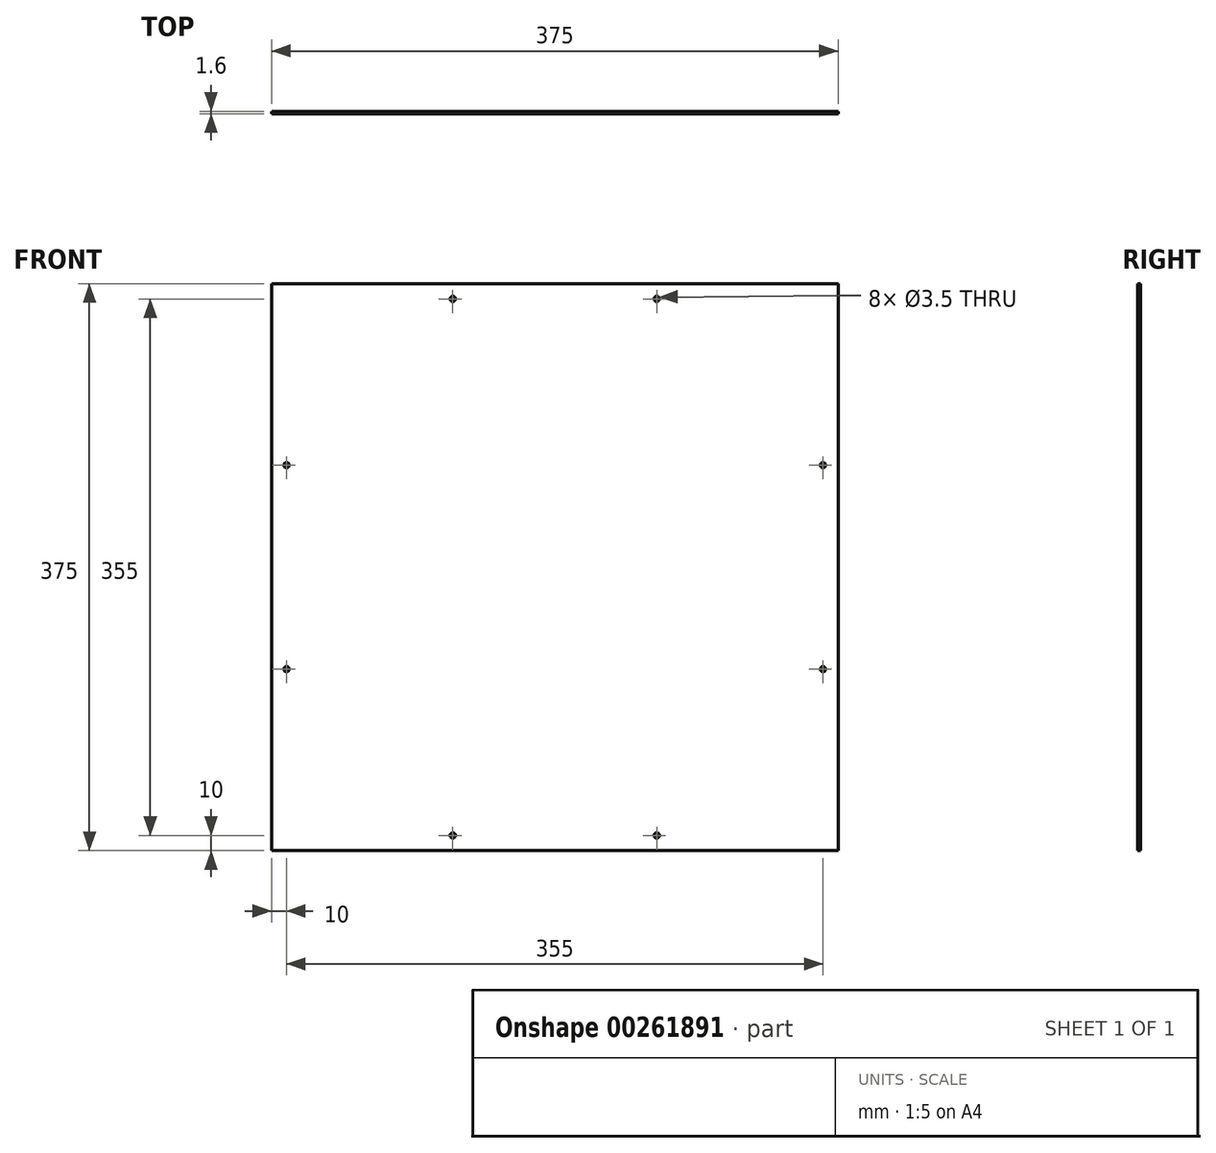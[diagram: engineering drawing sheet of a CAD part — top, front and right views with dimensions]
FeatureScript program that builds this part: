
annotation { "Feature Type Name" : "Feature", "Feature Type Description" : "" }
export const myFeature = defineFeature(function(context is Context, id is Id, definition is map)
    precondition{}
    {
        {
            var Q0;
            Q0=qCreatedBy(makeId("Front.planeOp"),FACE);
            var sketch = newSketch(context, id + "F0", { "sketchPlane" : qUnion([Q0])});
            skLineSegment(sketch, "E0.bottom", {"start": v(0, 0) * mm, "end": v(-375, 0) * mm});
            skLineSegment(sketch, "E0.top", {"start": v(0, 375) * mm, "end": v(-375, 375) * mm});
            skLineSegment(sketch, "E0.left", {"start": v(0, 0) * mm, "end": v(0, 375) * mm});
            skLineSegment(sketch, "E0.right", {"start": v(-375, 0) * mm, "end": v(-375, 375) * mm});
            skSolve(sketch);
        }
        {
            var Q0;
            Q0=makeQuery(id+"F0.imprint","IMPRINT",FACE,{"disambiguationData":[TD([[makeQuery(id+"F0.imprint","IMPRINT",EDGE,{"derivedFrom":sQuery(id+"F0.wireOp",EDGE,"E0.bottom")}),-1.0]])]});
            extrude(context, id + "F1", {"entities" : qUnion([Q0]), "depth" : 1.6 * mm});
        }
        {
            var Q0;
            Q0=makeQuery(id+"F1.opExtrude","CAP_FACE",FACE,{"disambiguationData":[OSD([sQuery(id+"F0.wireOp",EDGE,"E0.bottom"),sQuery(id+"F0.wireOp",EDGE,"E0.top"),sQuery(id+"F0.wireOp",EDGE,"E0.left"),sQuery(id+"F0.wireOp",EDGE,"E0.right")])],"isStart":false});
            var sketch = newSketch(context, id + "F2", { "sketchPlane" : qUnion([Q0])});
            skLineSegment(sketch, "E1.0.0", {"start": v(0, 0) * mm, "end": v(0, 375) * mm});
            skLineSegment(sketch, "E1.0.1", {"start": v(0, 375) * mm, "end": v(-375, 375) * mm});
            skLineSegment(sketch, "E1.0.2", {"start": v(-375, 375) * mm, "end": v(-375, 0) * mm});
            skLineSegment(sketch, "E1.0.3", {"start": v(-375, 0) * mm, "end": v(0, 0) * mm});
            skCircle(sketch, "E2", {"center": v(-10, 120) * mm, "radius": 1.75 * mm});
            skCircle(sketch, "E3", {"center": v(-10, 255) * mm, "radius": 1.75 * mm});
            skCircle(sketch, "E4", {"center": v(-120, 365) * mm, "radius": 1.75 * mm});
            skCircle(sketch, "E5", {"center": v(-255, 365) * mm, "radius": 1.75 * mm});
            skCircle(sketch, "E6", {"center": v(-365, 255) * mm, "radius": 1.75 * mm});
            skCircle(sketch, "E7", {"center": v(-365, 120) * mm, "radius": 1.75 * mm});
            skCircle(sketch, "E8", {"center": v(-255, 10) * mm, "radius": 1.75 * mm});
            skCircle(sketch, "E9", {"center": v(-120, 10) * mm, "radius": 1.75 * mm});
            skSolve(sketch);
        }
        {
            var Q0;
            Q0=makeQuery(id+"F2.imprint","IMPRINT",FACE,{"disambiguationData":[TD([[makeQuery(id+"F2.imprint","IMPRINT",EDGE,{"derivedFrom":sQuery(id+"F2.wireOp",EDGE,"E5")}),1.0]])]});
            var Q1;
            Q1=makeQuery(id+"F2.imprint","IMPRINT",FACE,{"disambiguationData":[TD([[makeQuery(id+"F2.imprint","IMPRINT",EDGE,{"derivedFrom":sQuery(id+"F2.wireOp",EDGE,"E4")}),1.0]])]});
            var Q2;
            Q2=makeQuery(id+"F2.imprint","IMPRINT",FACE,{"disambiguationData":[TD([[makeQuery(id+"F2.imprint","IMPRINT",EDGE,{"derivedFrom":sQuery(id+"F2.wireOp",EDGE,"E2")}),1.0]])]});
            var Q3;
            Q3=makeQuery(id+"F2.imprint","IMPRINT",FACE,{"disambiguationData":[TD([[makeQuery(id+"F2.imprint","IMPRINT",EDGE,{"derivedFrom":sQuery(id+"F2.wireOp",EDGE,"E7")}),1.0]])]});
            var Q4;
            Q4=makeQuery(id+"F2.imprint","IMPRINT",FACE,{"disambiguationData":[TD([[makeQuery(id+"F2.imprint","IMPRINT",EDGE,{"derivedFrom":sQuery(id+"F2.wireOp",EDGE,"E6")}),1.0]])]});
            var Q5;
            Q5=makeQuery(id+"F2.imprint","IMPRINT",FACE,{"disambiguationData":[TD([[makeQuery(id+"F2.imprint","IMPRINT",EDGE,{"derivedFrom":sQuery(id+"F2.wireOp",EDGE,"E3")}),1.0]])]});
            var Q6;
            Q6=makeQuery(id+"F2.imprint","IMPRINT",FACE,{"disambiguationData":[TD([[makeQuery(id+"F2.imprint","IMPRINT",EDGE,{"derivedFrom":sQuery(id+"F2.wireOp",EDGE,"E9")}),1.0]])]});
            var Q7;
            Q7=makeQuery(id+"F2.imprint","IMPRINT",FACE,{"disambiguationData":[TD([[makeQuery(id+"F2.imprint","IMPRINT",EDGE,{"derivedFrom":sQuery(id+"F2.wireOp",EDGE,"E8")}),1.0]])]});
            extrude(context, id + "F3", {"entities" : qUnion([Q0, Q1, Q2, Q3, Q4, Q5, Q6, Q7]), "operationType" : NewBodyOperationType.REMOVE, "oppositeDirection" : true, "depth" : 2 * mm});
        }
    });
